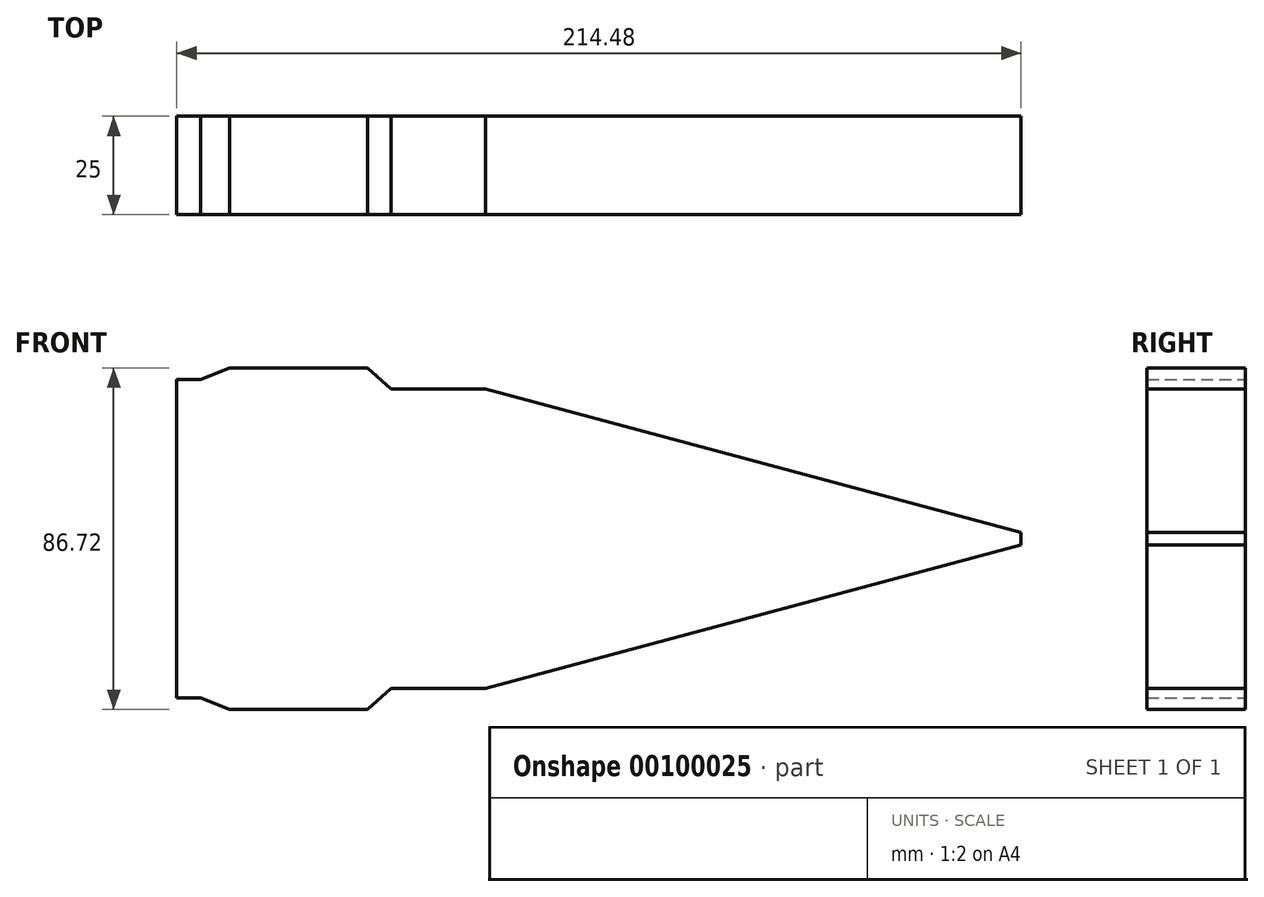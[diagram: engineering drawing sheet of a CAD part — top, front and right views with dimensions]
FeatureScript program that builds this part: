
annotation { "Feature Type Name" : "Feature", "Feature Type Description" : "" }
export const myFeature = defineFeature(function(context is Context, id is Id, definition is map)
    precondition{}
    {
        {
            var Q0;
            Q0=qCreatedBy(makeId("Front.planeOp"),FACE);
            var sketch = newSketch(context, id + "F0", { "sketchPlane" : qUnion([Q0])});
            skLineSegment(sketch, "E0", {"start": v(-59.47, 40.48) * mm, "end": v(-53.47, 40.48) * mm});
            skLineSegment(sketch, "E1", {"start": v(-53.47, 40.48) * mm, "end": v(-46, 43.36) * mm});
            skLineSegment(sketch, "E2", {"start": v(-46, 43.36) * mm, "end": v(-11, 43.36) * mm});
            skLineSegment(sketch, "E3", {"start": v(-11, 43.36) * mm, "end": v(-5.04, 38.03) * mm});
            skLineSegment(sketch, "E4", {"start": v(-5.04, 38.03) * mm, "end": v(18.96, 38.03) * mm});
            skLineSegment(sketch, "E5", {"start": v(18.96, 38.03) * mm, "end": v(155, 1.54) * mm});
            skLineSegment(sketch, "E6.MirrorCS", {"start": v(-59.47, -40.48) * mm, "end": v(-53.47, -40.48) * mm});
            skLineSegment(sketch, "E7.MirrorCS", {"start": v(-53.47, -40.48) * mm, "end": v(-46, -43.36) * mm});
            skLineSegment(sketch, "E8.MirrorCS", {"start": v(-46, -43.36) * mm, "end": v(-11, -43.36) * mm});
            skLineSegment(sketch, "E9.MirrorCS", {"start": v(-11, -43.36) * mm, "end": v(-5.04, -38.03) * mm});
            skLineSegment(sketch, "E10.MirrorCS", {"start": v(-5.04, -38.03) * mm, "end": v(18.96, -38.03) * mm});
            skLineSegment(sketch, "E11.MirrorCS", {"start": v(18.96, -38.03) * mm, "end": v(155, -1.54) * mm});
            skLineSegment(sketch, "E12", {"start": v(155, 1.54) * mm, "end": v(155, -1.54) * mm});
            skLineSegment(sketch, "E13", {"start": v(-59.47, 40.48) * mm, "end": v(-59.47, -40.48) * mm});
            skSolve(sketch);
        }
        {
            var Q0;
            Q0 = qSketchRegion(id + "F0", true);
            extrude(context, id + "F1", {"entities" : qUnion([Q0]), "depth" : 25 * mm});
        }
    });
